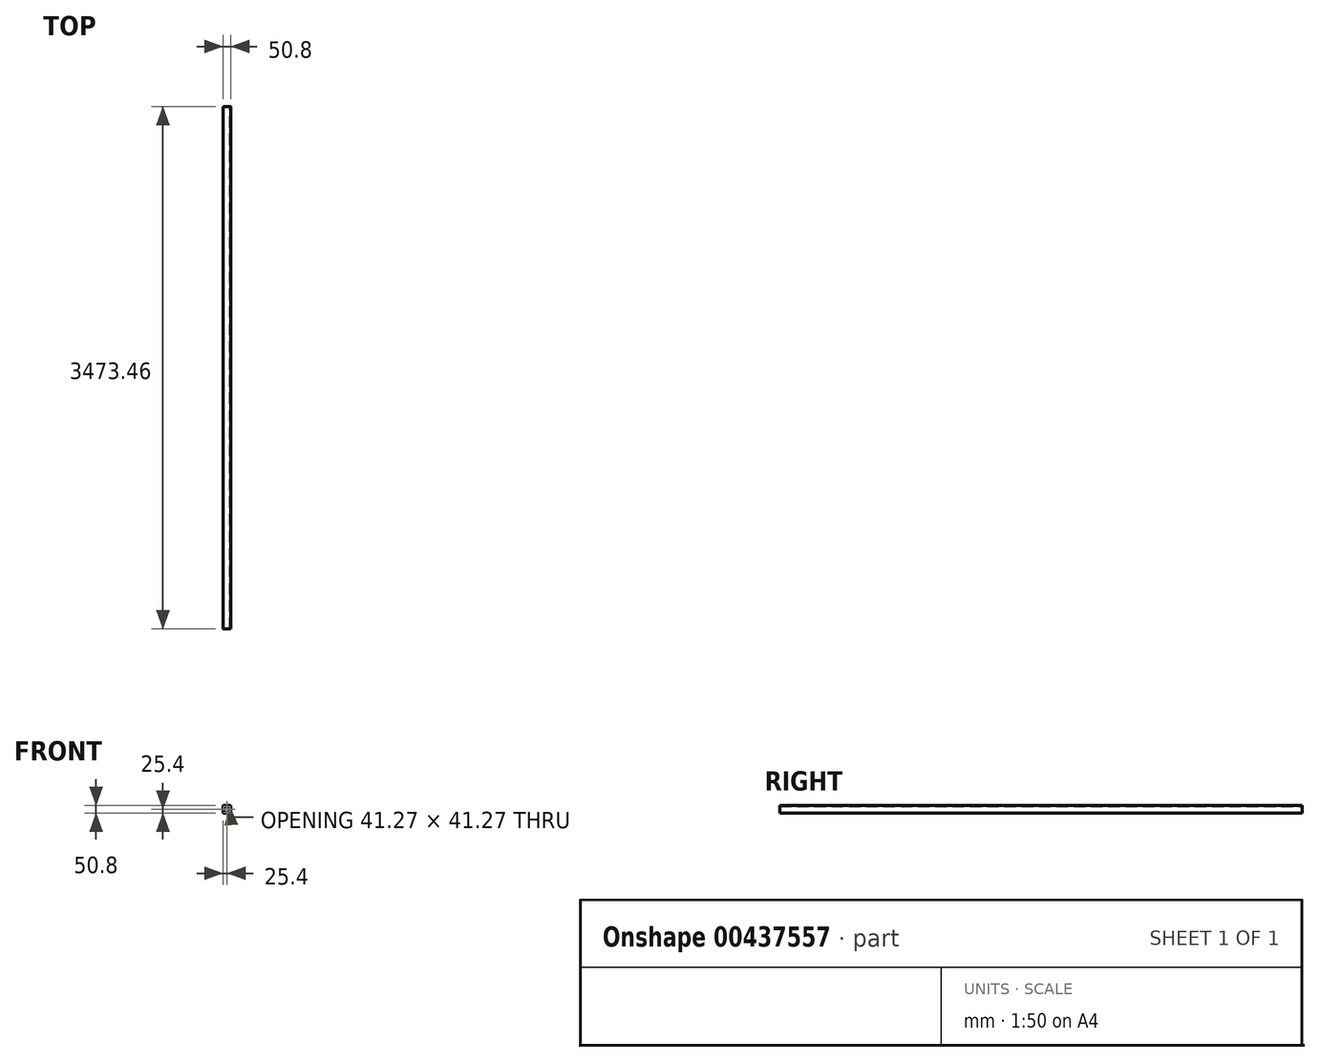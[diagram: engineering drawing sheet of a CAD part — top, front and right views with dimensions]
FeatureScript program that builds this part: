
annotation { "Feature Type Name" : "Feature", "Feature Type Description" : "" }
export const myFeature = defineFeature(function(context is Context, id is Id, definition is map)
    precondition{}
    {
        {
            var Q0;
            Q0=qCreatedBy(makeId("Front.planeOp"),FACE);
            var sketch = newSketch(context, id + "F0", { "sketchPlane" : qUnion([Q0])});
            skLineSegment(sketch, "E0.bottom", {"start": v(25.4, -25.4) * mm, "end": v(-25.4, -25.4) * mm});
            skLineSegment(sketch, "E0.top", {"start": v(25.4, 25.4) * mm, "end": v(-25.4, 25.4) * mm});
            skLineSegment(sketch, "E0.left", {"start": v(25.4, -25.4) * mm, "end": v(25.4, 25.4) * mm});
            skLineSegment(sketch, "E0.right", {"start": v(-25.4, -25.4) * mm, "end": v(-25.4, 25.4) * mm});
            skPoint(sketch, "E0.middle", {"position": v(0, 0) * mm});
            skLineSegment(sketch, "E1.bottom", {"start": v(20.64, -20.64) * mm, "end": v(-20.64, -20.64) * mm});
            skLineSegment(sketch, "E1.top", {"start": v(20.64, 20.64) * mm, "end": v(-20.64, 20.64) * mm});
            skLineSegment(sketch, "E1.left", {"start": v(20.64, -20.64) * mm, "end": v(20.64, 20.64) * mm});
            skLineSegment(sketch, "E1.right", {"start": v(-20.64, -20.64) * mm, "end": v(-20.64, 20.64) * mm});
            skSolve(sketch);
        }
        {
            var Q0;
            Q0 = qSketchRegion(id + "F0", true);
            extrude(context, id + "F1", {"entities" : qUnion([Q0]), "endBound" : BoundingType.SYMMETRIC, "depth" : 3473.45 * mm});
        }
        {
            var Q0;
            Q0=makeQuery(id+"F1.opExtrude","SWEPT_EDGE",EDGE,{"disambiguationData":[OSD([sQuery(id+"F0.wireOp",EDGE,"E0.top"),sQuery(id+"F0.wireOp",EDGE,"E0.right")])]});
            var Q1;
            Q1=makeQuery(id+"F1.opExtrude","SWEPT_EDGE",EDGE,{"disambiguationData":[OSD([sQuery(id+"F0.wireOp",EDGE,"E0.top"),sQuery(id+"F0.wireOp",EDGE,"E0.left")])]});
            var Q2;
            Q2=makeQuery(id+"F1.opExtrude","SWEPT_EDGE",EDGE,{"disambiguationData":[OSD([sQuery(id+"F0.wireOp",EDGE,"E1.bottom"),sQuery(id+"F0.wireOp",EDGE,"E1.right")])]});
            var Q3;
            Q3=makeQuery(id+"F1.opExtrude","SWEPT_EDGE",EDGE,{"disambiguationData":[OSD([sQuery(id+"F0.wireOp",EDGE,"E1.bottom"),sQuery(id+"F0.wireOp",EDGE,"E1.left")])]});
            var Q4;
            Q4=makeQuery(id+"F1.opExtrude","SWEPT_EDGE",EDGE,{"disambiguationData":[OSD([sQuery(id+"F0.wireOp",EDGE,"E0.bottom"),sQuery(id+"F0.wireOp",EDGE,"E0.left")])]});
            var Q5;
            Q5=makeQuery(id+"F1.opExtrude","SWEPT_EDGE",EDGE,{"disambiguationData":[OSD([sQuery(id+"F0.wireOp",EDGE,"E0.bottom"),sQuery(id+"F0.wireOp",EDGE,"E0.right")])]});
            fillet(context, id + "F2", {"entities" : qUnion([Q0, Q1, Q2, Q3, Q4, Q5]), "radius" : 5.08 * mm, "tangentPropagation" : true, "allowEdgeOverflow" : false});
        }
    });
